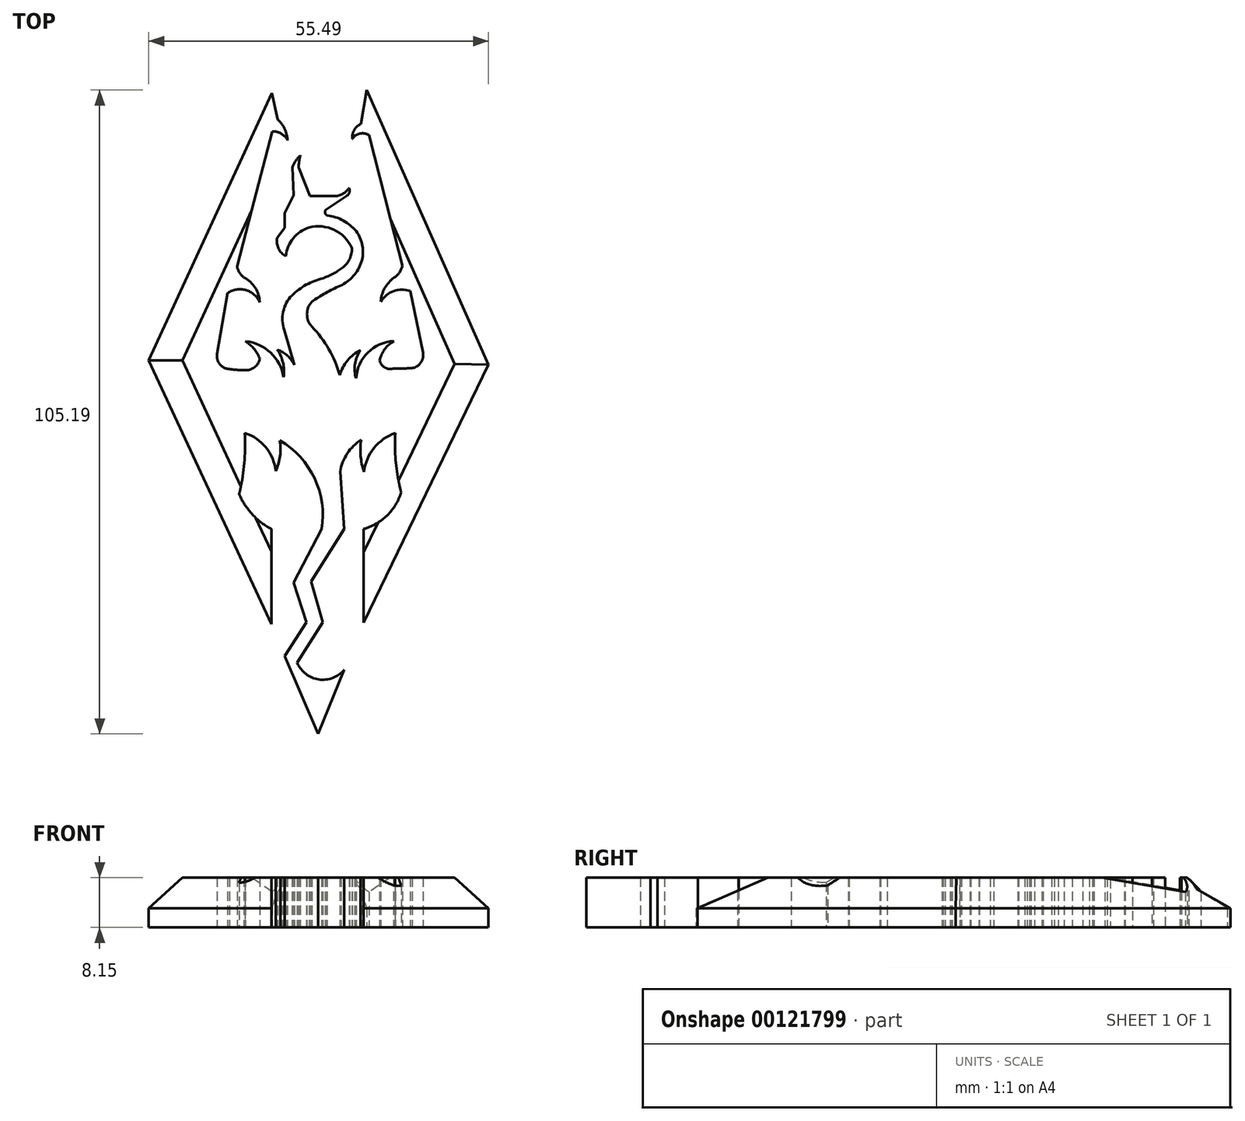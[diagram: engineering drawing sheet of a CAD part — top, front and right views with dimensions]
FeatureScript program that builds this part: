
annotation { "Feature Type Name" : "Feature", "Feature Type Description" : "" }
export const myFeature = defineFeature(function(context is Context, id is Id, definition is map)
    precondition{}
    {
        {
            var Q0;
            Q0=qCreatedBy(makeId("Top.planeOp"),FACE);
            var sketch = newSketch(context, id + "F0", { "sketchPlane" : qUnion([Q0])});
            skLineSegment(sketch, "E0", {"start": v(-11.78, 55.6) * mm, "end": v(-31.92, 11.9) * mm});
            skLineSegment(sketch, "E1", {"start": v(-31.92, 11.9) * mm, "end": v(-11.9, -31.25) * mm});
            skLineSegment(sketch, "E2", {"start": v(-11.9, -31.25) * mm, "end": v(-11.9, -15.67) * mm});
            skLineSegment(sketch, "E3", {"start": v(3.15, -15.67) * mm, "end": v(3.15, -30.98) * mm});
            skLineSegment(sketch, "E4", {"start": v(3.15, -30.98) * mm, "end": v(23.57, 11.2) * mm});
            skLineSegment(sketch, "E5", {"start": v(23.57, 11.2) * mm, "end": v(3.69, 56.06) * mm});
            skLineSegment(sketch, "E6", {"start": v(-8.22, -24.44) * mm, "end": v(-3.66, -15.7) * mm});
            skLineSegment(sketch, "E7", {"start": v(-8.22, -24.44) * mm, "end": v(-6.13, -30.9) * mm});
            skLineSegment(sketch, "E8", {"start": v(-6.13, -30.9) * mm, "end": v(-9.74, -36.4) * mm});
            skLineSegment(sketch, "E9", {"start": v(-9.74, -36.4) * mm, "end": v(-4.23, -49.13) * mm});
            skLineSegment(sketch, "E10", {"start": v(10.77, 23.24) * mm, "end": v(12.86, 13.18) * mm});
            skLineSegment(sketch, "E11", {"start": v(0, -38.68) * mm, "end": v(-4.23, -49.13) * mm});
            skLineSegment(sketch, "E12", {"start": v(-19.05, 22.86) * mm, "end": v(-20.76, 12.99) * mm});
            skLineSegment(sketch, "E13", {"start": v(-5.37, -24.25) * mm, "end": v(-3.47, -30.9) * mm});
            skLineSegment(sketch, "E14", {"start": v(-3.47, -30.9) * mm, "end": v(-7.65, -37.54) * mm});
            skLineSegment(sketch, "E15", {"start": v(3.69, 56.06) * mm, "end": v(2.71, 50.5) * mm});
            skLineSegment(sketch, "E16", {"start": v(-11.78, 55.6) * mm, "end": v(-10.86, 51.26) * mm});
            skLineSegment(sketch, "E17", {"start": v(4.07, 48.7) * mm, "end": v(9.5, 27.29) * mm});
            skLineSegment(sketch, "E18", {"start": v(-11.76, 49.3) * mm, "end": v(-17.49, 27.29) * mm});
            skLineSegment(sketch, "E19", {"start": v(-5.37, -24.25) * mm, "end": v(0, -15.7) * mm});
            skLineSegment(sketch, "E20", {"start": v(0, -15.7) * mm, "end": v(-0.65, -6.28) * mm});
            skArc(sketch, "E21", {"start": v(-17.16, -9.98) * mm, "mid": v(-15, -13.27) * mm, "end": v(-11.9, -15.67) * mm});
            skArc(sketch, "E22", {"start": v(3.15, -15.67) * mm, "mid": v(7, -13.47) * mm, "end": v(9.31, -9.7) * mm});
            skArc(sketch, "E23", {"start": v(-7.65, -37.54) * mm, "mid": v(-4.14, -40.25) * mm, "end": v(0, -38.68) * mm});
            skArc(sketch, "E24", {"start": v(-3.66, -15.7) * mm, "mid": v(-4.84, -7.38) * mm, "end": v(-10.52, -1.2) * mm});
            skArc(sketch, "E25", {"start": v(-17.16, -9.98) * mm, "mid": v(-16.32, -5.03) * mm, "end": v(-16.22, 0) * mm});
            skArc(sketch, "E26", {"start": v(-11.19, -6.18) * mm, "mid": v(-12.78, -2.34) * mm, "end": v(-16.22, 0) * mm});
            skArc(sketch, "E27", {"start": v(-11.19, -6.18) * mm, "mid": v(-10.46, -3.74) * mm, "end": v(-10.52, -1.2) * mm});
            skArc(sketch, "E28", {"start": v(2.78, -1.08) * mm, "mid": v(0.5, -3.31) * mm, "end": v(-0.65, -6.28) * mm});
            skArc(sketch, "E29", {"start": v(2.78, -1.08) * mm, "mid": v(2.7, -3.72) * mm, "end": v(3.25, -6.31) * mm});
            skArc(sketch, "E30", {"start": v(8.36, 0) * mm, "mid": v(4.88, -2.41) * mm, "end": v(3.25, -6.31) * mm});
            skArc(sketch, "E31", {"start": v(8.36, 0) * mm, "mid": v(8.46, -4.89) * mm, "end": v(9.31, -9.7) * mm});
            skArc(sketch, "E32", {"start": v(-20.76, 12.99) * mm, "mid": v(-20.31, 11.27) * mm, "end": v(-18.73, 10.46) * mm});
            skArc(sketch, "E33", {"start": v(-13.78, 12.11) * mm, "mid": v(-14.7, 13.75) * mm, "end": v(-16.1, 15) * mm});
            skArc(sketch, "E34", {"start": v(-16.27, 10.3) * mm, "mid": v(-14.7, 10.74) * mm, "end": v(-13.78, 12.11) * mm});
            skArc(sketch, "E35", {"start": v(-18.73, 10.46) * mm, "mid": v(-17.5, 10.33) * mm, "end": v(-16.27, 10.3) * mm});
            skArc(sketch, "E36", {"start": v(-9.89, 9.15) * mm, "mid": v(-12, 13.14) * mm, "end": v(-16.1, 15) * mm});
            skArc(sketch, "E37", {"start": v(-9.89, 9.15) * mm, "mid": v(-9.99, 11.5) * mm, "end": v(-10.94, 13.64) * mm});
            skArc(sketch, "E38", {"start": v(-8.1, 11.14) * mm, "mid": v(-9.27, 12.68) * mm, "end": v(-10.94, 13.64) * mm});
            skArc(sketch, "E39", {"start": v(2.68, 13.55) * mm, "mid": v(0.55, 11.86) * mm, "end": v(-0.7, 9.45) * mm});
            skArc(sketch, "E40", {"start": v(2.68, 13.55) * mm, "mid": v(1.76, 11.33) * mm, "end": v(1.96, 8.94) * mm});
            skArc(sketch, "E41", {"start": v(8.14, 15.03) * mm, "mid": v(3.87, 13.18) * mm, "end": v(1.96, 8.94) * mm});
            skArc(sketch, "E42", {"start": v(8.14, 15.03) * mm, "mid": v(6.62, 13.7) * mm, "end": v(5.81, 11.86) * mm});
            skArc(sketch, "E43", {"start": v(5.81, 11.86) * mm, "mid": v(6.65, 10.72) * mm, "end": v(8.05, 10.55) * mm});
            skArc(sketch, "E44", {"start": v(11.14, 10.63) * mm, "mid": v(12.54, 11.54) * mm, "end": v(12.86, 13.18) * mm});
            skArc(sketch, "E45", {"start": v(8.05, 10.55) * mm, "mid": v(9.6, 10.56) * mm, "end": v(11.14, 10.63) * mm});
            skArc(sketch, "E46", {"start": v(10.77, 23.24) * mm, "mid": v(8.08, 23.2) * mm, "end": v(5.98, 21.5) * mm});
            skArc(sketch, "E47", {"start": v(8.13, 25.39) * mm, "mid": v(6.62, 23.68) * mm, "end": v(5.98, 21.5) * mm});
            skArc(sketch, "E48", {"start": v(8.13, 25.39) * mm, "mid": v(9, 26.2) * mm, "end": v(9.5, 27.29) * mm});
            skArc(sketch, "E49", {"start": v(-17.49, 27.29) * mm, "mid": v(-17.1, 26.25) * mm, "end": v(-16.35, 25.44) * mm});
            skArc(sketch, "E50", {"start": v(-13.79, 21.38) * mm, "mid": v(-14.53, 23.75) * mm, "end": v(-16.35, 25.44) * mm});
            skArc(sketch, "E51", {"start": v(-13.79, 21.38) * mm, "mid": v(-16.06, 23.38) * mm, "end": v(-19.05, 22.86) * mm});
            skLineSegment(sketch, "E52", {"start": v(-7.4, 43.25) * mm, "end": v(-5.59, 38.73) * mm});
            skLineSegment(sketch, "E53", {"start": v(-5.59, 38.73) * mm, "end": v(-1.67, 38.73) * mm});
            skLineSegment(sketch, "E54", {"start": v(-3.02, 36.47) * mm, "end": v(0.4, 38.73) * mm});
            skLineSegment(sketch, "E55", {"start": v(-8.43, 43.48) * mm, "end": v(-8.25, 38.89) * mm});
            skLineSegment(sketch, "E56", {"start": v(-8.25, 38.89) * mm, "end": v(-9.71, 35.94) * mm});
            skLineSegment(sketch, "E57", {"start": v(-9.71, 35.94) * mm, "end": v(-9.71, 33.52) * mm});
            skLineSegment(sketch, "E58", {"start": v(-9.71, 33.52) * mm, "end": v(-10.9, 31.93) * mm});
            skArc(sketch, "E59", {"start": v(-9.24, 47.86) * mm, "mid": v(-9.72, 49.71) * mm, "end": v(-10.86, 51.26) * mm});
            skArc(sketch, "E60", {"start": v(-9.24, 47.86) * mm, "mid": v(-10.28, 48.95) * mm, "end": v(-11.76, 49.3) * mm});
            skArc(sketch, "E61", {"start": v(2.71, 50.5) * mm, "mid": v(1.61, 49.51) * mm, "end": v(1.34, 48.06) * mm});
            skArc(sketch, "E62", {"start": v(4.07, 48.7) * mm, "mid": v(2.57, 48.96) * mm, "end": v(1.34, 48.06) * mm});
            skArc(sketch, "E63", {"start": v(-1.67, 38.73) * mm, "mid": v(-0.26, 39.08) * mm, "end": v(0.8, 40.07) * mm});
            skArc(sketch, "E64", {"start": v(0.4, 38.73) * mm, "mid": v(0.84, 39.33) * mm, "end": v(0.8, 40.07) * mm});
            skArc(sketch, "E65", {"start": v(-7.14, 45.4) * mm, "mid": v(-7.9, 44.51) * mm, "end": v(-8.43, 43.48) * mm});
            skArc(sketch, "E66", {"start": v(-7.14, 45.4) * mm, "mid": v(-7.37, 44.34) * mm, "end": v(-7.4, 43.25) * mm});
            skArc(sketch, "E67", {"start": v(-10.9, 31.93) * mm, "mid": v(-10.73, 30.19) * mm, "end": v(-9.5, 28.94) * mm});
            skArc(sketch, "E68", {"start": v(-5.73, 33.61) * mm, "mid": v(-8.33, 31.85) * mm, "end": v(-9.5, 28.94) * mm});
            skArc(sketch, "E69", {"start": v(1.25, 30.27) * mm, "mid": v(-1.63, 33.21) * mm, "end": v(-5.73, 33.61) * mm});
            skArc(sketch, "E70", {"start": v(-0.53, 26.85) * mm, "mid": v(0.83, 28.3) * mm, "end": v(1.25, 30.27) * mm});
            skArc(sketch, "E71", {"start": v(-3.48, 25.3) * mm, "mid": v(-1.95, 25.96) * mm, "end": v(-0.53, 26.85) * mm});
            skArc(sketch, "E72", {"start": v(-3.48, 25.3) * mm, "mid": v(-6.2, 24.24) * mm, "end": v(-8.53, 22.5) * mm});
            skArc(sketch, "E73", {"start": v(-8.53, 22.5) * mm, "mid": v(-9.95, 19.84) * mm, "end": v(-9.77, 16.83) * mm});
            skLineSegment(sketch, "E74", {"start": v(-9.77, 16.83) * mm, "end": v(-8.1, 11.14) * mm});
            skArc(sketch, "E75", {"start": v(-3.02, 36.47) * mm, "mid": v(-3.11, 35.97) * mm, "end": v(-2.77, 35.6) * mm});
            skArc(sketch, "E76", {"start": v(1.96, 33) * mm, "mid": v(-0.17, 34.73) * mm, "end": v(-2.77, 35.6) * mm});
            skArc(sketch, "E77", {"start": v(2.81, 27.93) * mm, "mid": v(3, 30.57) * mm, "end": v(1.96, 33) * mm});
            skArc(sketch, "E78", {"start": v(-0.64, 24.08) * mm, "mid": v(1.48, 25.65) * mm, "end": v(2.81, 27.93) * mm});
            skArc(sketch, "E79", {"start": v(-0.64, 24.08) * mm, "mid": v(-3.04, 22.9) * mm, "end": v(-5.3, 21.45) * mm});
            skArc(sketch, "E80", {"start": v(-5.3, 21.45) * mm, "mid": v(-6.07, 19.44) * mm, "end": v(-5.3, 17.42) * mm});
            skArc(sketch, "E81", {"start": v(-0.7, 9.45) * mm, "mid": v(-2.5, 13.72) * mm, "end": v(-5.3, 17.42) * mm});
            skSolve(sketch);
        }
        {
            var Q0;
            Q0=makeQuery(id+"F0.imprint","IMPRINT",FACE,{"disambiguationData":[TD([[makeQuery(id+"F0.imprint","IMPRINT",EDGE,{"derivedFrom":sQuery(id+"F0.wireOp",EDGE,"E0")}),1.0]])]});
            extrude(context, id + "F1", {"entities" : qUnion([Q0]), "depth" : 8.15 * mm});
        }
        {
            var Q0;
            Q0=makeQuery(id+"F1.opExtrude","CAP_EDGE",EDGE,{"disambiguationData":[OSD([sQuery(id+"F0.wireOp",EDGE,"E0")])],"isStart":false});
            var Q1;
            Q1=makeQuery(id+"F1.opExtrude","CAP_EDGE",EDGE,{"disambiguationData":[OSD([sQuery(id+"F0.wireOp",EDGE,"E1")])],"isStart":false});
            var Q2;
            Q2=makeQuery(id+"F1.opExtrude","CAP_EDGE",EDGE,{"disambiguationData":[OSD([sQuery(id+"F0.wireOp",EDGE,"E5")])],"isStart":false});
            var Q3;
            Q3=makeQuery(id+"F1.opExtrude","CAP_EDGE",EDGE,{"disambiguationData":[OSD([sQuery(id+"F0.wireOp",EDGE,"E4")])],"isStart":false});
            chamfer(context, id + "F2", {"entities" : qUnion([Q0, Q1, Q2, Q3]), "width" : 5 * mm, "tangentPropagation" : true});
        }
    });
